# Revit family: Shower-Body_Spray-KOHLER-K-26299T_1
name_source: partatom
category: Plumbing Fixtures
revit_build: Autodesk Revit 2017 (Build: 20160225_1515(x64)
units: mm (PartAtom-declared; Revit-internal decimal feet)

## family parameters
Cut with Voids When Loaded = No
Host = Face
OmniClass Number = 23.31.17.00
OmniClass Title = Showers
Part Type = Normal
Room Calculation Point = No
Round Connector Dimension = Use Diameter
Shared = No

## types (6) — shared parameters
ADA Compliant = No
Assembly Code = D2010700
CW Connection = No
Cold Water Inlet = Cold Water Inlet
Date Modified = 02/04/2021
Default Elevation = 42"
Description = Round Rotator Body Spray
Drain Included = No
Flow Rate = 3 GPM
HW Connection = Yes
Height = 2 3/4"
Hot Water Inlet = Tempered Water Inlet
Length = 2 1/8"
Manufacturer = KOHLER Co.
Master Format 2014 = 22 42 23
Master Format 2014 Name = Residential Showers
Material = Plastic
Pressure = 80.00 psi
URL = http://www.kohler.com.cn
Vent Connection = No
Waste Connection = No
Waste Water Outlet = Waste Water Outlet
WaterSense Certified = No
Width = 2 3/4"

## per-type parameters (varying)
| type | Finish | Model | Type |
| CP-Polished Chrome | KOHLER-Plastic-CP-Polished_Chrome | K-26299T-CP | 1 |
| BN-Vibrant Brushed Nickel | KOHLER-Plastic-BN-Vibrant_Brushed_Nickel | K-26299T-BN | 2 |
| BL-Matte Black | KOHLER-Plastic-BL-Matte_Black | K-26299T-BL | 3 |
| AF-Vibrant French Gold | KOHLER-Plastic-AF-Vibrant_French_Gold | K-26299T-AF | 4 |
| RGD-Rose Gold | Kohler-Plastic-RGD-Rose_Gold | K-26299T-RGD | 5 |
| 2MB-Vibrant Brushed Moderne Brass | KOHLER-Plastic-2MB-Vibrant_Brushed_Moderne_Brass | K-26299T-2MB | 6 |

## geometry (parser evidence)
native form markers: Sweep x5
no freeform markers — native parametric forms only
